# Revit family: BS-678AB-EB
name_source: partatom
category: Communication Devices
units: mm (PartAtom-declared; Revit-internal decimal feet)

## family parameters
Always vertical = No
Cut with Voids When Loaded = No
Maintain Annotation Orientation = No
Part Type = Normal
Room Calculation Point = No
Round Connector Dimension = Use Diameter
Shared = No
Work Plane-Based = Yes

## types (1)
- BS-678AB-EB
    Accessory = Speaker mounting screw x2, Baffle fixing screw x2
    Applicable Cable Size = Outer diameter : Max. Ø10 mm (for exposed wiring)
                Ø6.5 - Ø12.5 mm (for in-wall wiring)
Conductor : Solid wire or 7-core wire
No bridge connection : 0.8 - 10 mm  (AWG18 - AWG7) for solid wire
                      0.8 - 8 mm  (AWG18 - AWG8) for 7-core wire
Bridge connection : 0.8 - 2.5 mm  (AWG18 - AWG13) for solid wire
                      0.8 - 1.5 mm  (AWG18 - AWG15) for 7-core wire
    Connection = 2x 3-pins screw steatite terminal
    Coverage Angle = Horizontal: 225° (500 Hz), 125° (1 kHz), 60° (2 kHz), 35° (4 kHz)
Vertical  : 240° (500 Hz), 200° (1 kHz), 125° (2 kHz), 110° (4 kHz)
    Default Elevation = 1200 mm
    Dimension = 190 (W) x 250 (H) x 110 (D) mm (7.48" x 9.84" x 4.33")
    Environmental Type = A (indoor applications)
    Finish = Baffle: HIPS resin, white (RAL 9010 or equivalent color)
Cabinet: Particle board with pvc sheet, white (RAL 9010 or equivalent color)
Grille: Surface-treated steel plate net, white (RAL 9010 or equivalent color), paint
    Frequency Response = 155 Hz - 20 kHz (Peak -20 dB )
    Manufacturer = TOA
    Model = BS-678AB-EB
    Operating Temperature = -10 °C to +55 °C (14 °F to 122 °F)
    Rated Impedance = 100 V line: 1.7 kΩ (6 W), 3.3 kΩ (3 W), 6.7 kΩ (1.5 W)
    Rated Input = 2 x 6 W (100 V line)
    Sensitivity (SPL) Max. SPL = 92 dB (2x 0.5 W, 1 m) (100 Hz - 10 kHz, pink noise)
102 dB (2x 6 W, 1 m) (100 Hz - 10 kHz, pink noise)
    Sensitivity EN54-24 Max. Sensitivity EN54-24 = 80 dB (2x 0.5 W, 4 m) (100 Hz - 10 kHz, pink noise)
90 dB (2x 6 W, 4 m) (100 Hz - 10 kHz, pink noise)
    Speaker Component = 2x 10 cm (4") double cone-type
    Speaker Mounting Method = Wall-mount
    Update info = https://www.sound-toa.com
    Ver = 1.0
    Weight = 2.3 kg (5.07 lb)
    Weight [Kg] (for Schedules/Quantities) = 2.3

## geometry (parser evidence)
native form markers: Sweep x23
no freeform markers — native parametric forms only
